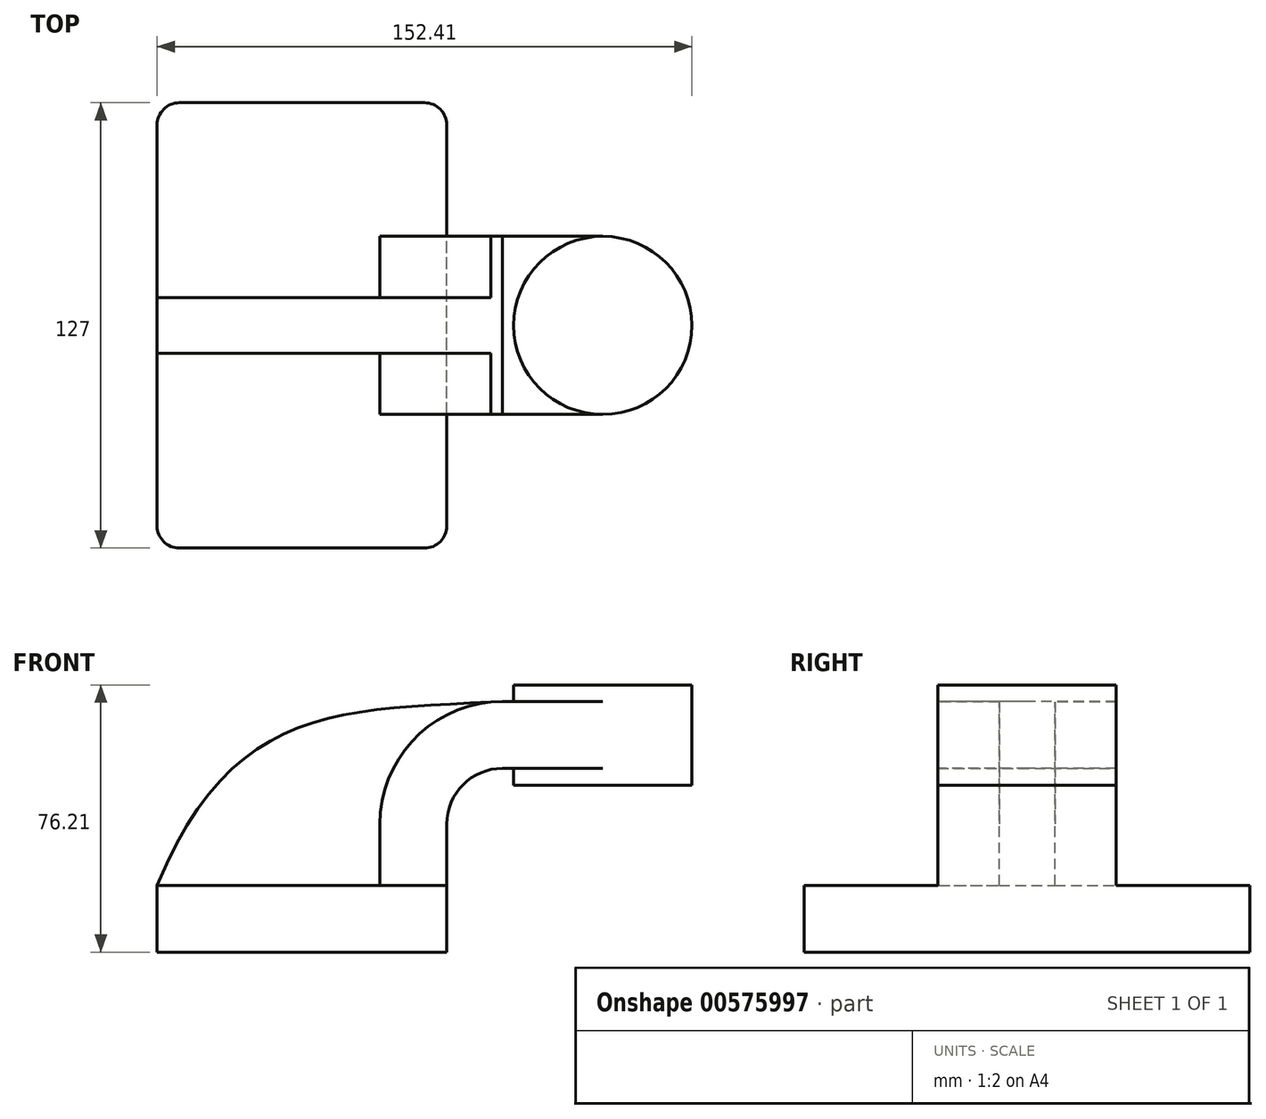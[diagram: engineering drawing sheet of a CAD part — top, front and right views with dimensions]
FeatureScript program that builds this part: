
annotation { "Feature Type Name" : "Feature", "Feature Type Description" : "" }
export const myFeature = defineFeature(function(context is Context, id is Id, definition is map)
    precondition{}
    {
        {
            var Q0;
            Q0=qCreatedBy(makeId("Front.planeOp"),FACE);
            var sketch = newSketch(context, id + "F0", { "sketchPlane" : qUnion([Q0])});
            skLineSegment(sketch, "E0.bottom", {"start": v(-41.28, -9.52) * mm, "end": v(41.28, -9.52) * mm});
            skLineSegment(sketch, "E0.top", {"start": v(-41.28, 9.53) * mm, "end": v(41.28, 9.53) * mm});
            skLineSegment(sketch, "E0.left", {"start": v(-41.27, -9.52) * mm, "end": v(-41.28, 9.53) * mm});
            skLineSegment(sketch, "E0.right", {"start": v(41.28, -9.52) * mm, "end": v(41.28, 9.53) * mm});
            skPoint(sketch, "E0.middle", {"position": v(0, 0) * mm});
            skLineSegment(sketch, "E1.bottom", {"start": v(60.32, 38.1) * mm, "end": v(111.12, 38.1) * mm});
            skLineSegment(sketch, "E1.top", {"start": v(60.32, 66.68) * mm, "end": v(111.12, 66.68) * mm});
            skLineSegment(sketch, "E1.left", {"start": v(60.32, 38.1) * mm, "end": v(60.32, 66.68) * mm});
            skLineSegment(sketch, "E1.right", {"start": v(111.12, 38.1) * mm, "end": v(111.12, 66.68) * mm});
            skPoint(sketch, "E1.middle", {"position": v(85.72, 52.39) * mm});
            skLineSegment(sketch, "E2", {"start": v(41.27, 9.53) * mm, "end": v(41.27, 27) * mm});
            skArc(sketch, "E3", {"start": v(41.27, 27) * mm, "mid": v(45.92, 38.23) * mm, "end": v(57.15, 42.88) * mm});
            skLineSegment(sketch, "E4", {"start": v(57.15, 42.88) * mm, "end": v(126.74, 42.88) * mm});
            skLineSegment(sketch, "E5.0", {"start": v(57.15, 61.93) * mm, "end": v(126.74, 61.93) * mm});
            skArc(sketch, "E5.1", {"start": v(22.22, 27) * mm, "mid": v(32.45, 51.7) * mm, "end": v(57.15, 61.93) * mm});
            skLineSegment(sketch, "E5.2", {"start": v(22.22, 9.53) * mm, "end": v(22.22, 27) * mm});
            skLineSegment(sketch, "E6", {"start": v(85.72, 38.1) * mm, "end": v(85.72, 66.68) * mm});
            skFitSpline(sketch, "E7", {"points": [v(-41.28, 9.53) * mm, v(57.15, 61.93) * mm], "startDerivative": vector(63.7, 153.2) * mm, "endDerivative": vector(143.9, 6.92) * mm});
            skSolve(sketch);
        }
        {
            var Q0;
            Q0=makeQuery(id+"F0.imprint","IMPRINT",FACE,{"disambiguationData":[TD([[makeQuery(id+"F0.imprint","IMPRINT",EDGE,{"derivedFrom":sQuery(id+"F0.wireOp",EDGE,"E0.bottom")}),1.0]])]});
            extrude(context, id + "F1", {"entities" : qUnion([Q0]), "endBound" : BoundingType.SYMMETRIC, "depth" : 127 * mm, "offsetDistance" : 25.4 * mm});
        }
        {
            var Q0;
            {var subQ1=sQuery(id+"F0.wireOp",EDGE,"E2");Q0=makeQuery(id+"F0.imprint","IMPRINT",FACE,{"disambiguationData":[TD([[makeQuery(id+"F0.imprint","IMPRINT",EDGE,{"derivedFrom":subQ1}),1.0]])]});}
            var Q1;
            {var subQ0=sQuery(id+"F0.wireOp",EDGE,"E4");var subQ1=sQuery(id+"F0.wireOp",EDGE,"E1.left");var subQ2=makeQuery(id+"F0.imprint","INTERSECT",VERTEX,{"derivedFrom":[subQ1,subQ0]});Q1=makeQuery(id+"F0.imprint","IMPRINT",FACE,{"disambiguationData":[TD([[makeQuery(id+"F0.imprint","IMPRINT",EDGE,{"disambiguationData":[TD([[subQ2,-1.0]])],"derivedFrom":subQ1}),-1.0]])]});}
            extrude(context, id + "F2", {"entities" : qUnion([Q0, Q1]), "operationType" : NewBodyOperationType.ADD, "endBound" : BoundingType.SYMMETRIC, "depth" : 50.8 * mm, "offsetDistance" : 25.4 * mm});
        }
        {
            var Q0;
            {var subQ0=sQuery(id+"F0.wireOp",EDGE,"E1.right");var subQ1=sQuery(id+"F0.wireOp",EDGE,"E1.top");var subQ2=makeQuery(id+"F0.imprint","INTERSECT",VERTEX,{"derivedFrom":[subQ1,subQ0]});Q0=makeQuery(id+"F0.imprint","IMPRINT",FACE,{"disambiguationData":[TD([[makeQuery(id+"F0.imprint","IMPRINT",EDGE,{"disambiguationData":[TD([[subQ2,1.0]])],"derivedFrom":subQ1}),-1.0]])]});}
            var Q1;
            {var subQ0=sQuery(id+"F0.wireOp",EDGE,"E1.right");var subQ1=sQuery(id+"F0.wireOp",EDGE,"E1.bottom");var subQ2=makeQuery(id+"F0.imprint","INTERSECT",VERTEX,{"derivedFrom":[subQ1,subQ0]});Q1=makeQuery(id+"F0.imprint","IMPRINT",FACE,{"disambiguationData":[TD([[makeQuery(id+"F0.imprint","IMPRINT",EDGE,{"disambiguationData":[TD([[subQ2,1.0]])],"derivedFrom":subQ1}),1.0]])]});}
            var Q2;
            {var subQ0=sQuery(id+"F0.wireOp",EDGE,"E4");var subQ1=sQuery(id+"F0.wireOp",EDGE,"E1.right");var subQ2=makeQuery(id+"F0.imprint","INTERSECT",VERTEX,{"derivedFrom":[subQ1,subQ0]});Q2=makeQuery(id+"F0.imprint","IMPRINT",FACE,{"disambiguationData":[TD([[makeQuery(id+"F0.imprint","IMPRINT",EDGE,{"disambiguationData":[TD([[subQ2,-1.0]])],"derivedFrom":subQ1}),1.0]])]});}
            var Q3;
            Q3=sQuery(id+"F0.wireOp",EDGE,"E6");
            revolve(context, id + "F3", {"operationType" : NewBodyOperationType.ADD, "entities" : qUnion([Q0, Q1, Q2]), "axis" : qUnion([Q3]), "revolveType" : RevolveType.FULL});
        }
        {
            var Q0;
            {var subQ3=sQuery(id+"F0.wireOp",EDGE,"E5.2");Q0=makeQuery(id+"F0.imprint","IMPRINT",FACE,{"disambiguationData":[TD([[makeQuery(id+"F0.imprint","IMPRINT",EDGE,{"derivedFrom":subQ3}),1.0]])]});}
            extrude(context, id + "F4", {"entities" : qUnion([Q0]), "operationType" : NewBodyOperationType.ADD, "endBound" : BoundingType.SYMMETRIC, "depth" : 15.88 * mm, "offsetDistance" : 25.4 * mm});
        }
        {
            var Q0;
            Q0=makeQuery(id+"F1.opExtrude","CAP_EDGE",EDGE,{"disambiguationData":[OSD([sQuery(id+"F0.wireOp",EDGE,"E0.right")])],"isStart":false});
            var Q1;
            Q1=makeQuery(id+"F1.opExtrude","CAP_EDGE",EDGE,{"disambiguationData":[OSD([sQuery(id+"F0.wireOp",EDGE,"E0.left")])],"isStart":false});
            var Q2;
            Q2=makeQuery(id+"F1.opExtrude","CAP_EDGE",EDGE,{"disambiguationData":[OSD([sQuery(id+"F0.wireOp",EDGE,"E0.right")])],"isStart":true});
            var Q3;
            Q3=makeQuery(id+"F1.opExtrude","CAP_EDGE",EDGE,{"disambiguationData":[OSD([sQuery(id+"F0.wireOp",EDGE,"E0.left")])],"isStart":true});
            fillet(context, id + "F5", {"entities" : qUnion([Q0, Q1, Q2, Q3]), "radius" : 6.35 * mm, "tangentPropagation" : true, "allowEdgeOverflow" : false});
        }
    });
